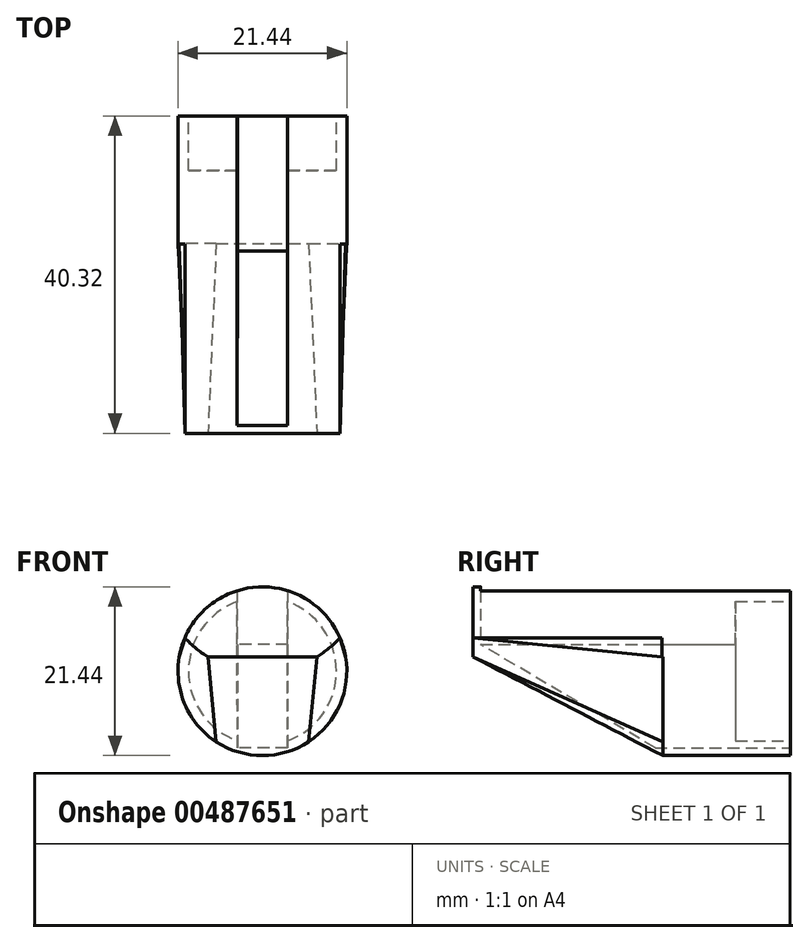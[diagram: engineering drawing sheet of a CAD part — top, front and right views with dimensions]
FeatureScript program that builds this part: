
annotation { "Feature Type Name" : "Feature", "Feature Type Description" : "" }
export const myFeature = defineFeature(function(context is Context, id is Id, definition is map)
    precondition{}
    {
        {
            var Q0;
            Q0=qCreatedBy(makeId("Front.planeOp"),FACE);
            var sketch = newSketch(context, id + "F0", { "sketchPlane" : qUnion([Q0])});
            skCircle(sketch, "E0", {"center": v(0, 0) * mm, "radius": 10.72 * mm});
            skSolve(sketch);
        }
        {
            var Q0;
            Q0=makeQuery(id+"F0.imprint","IMPRINT",FACE,{"disambiguationData":[TD([[makeQuery(id+"F0.imprint","IMPRINT",EDGE,{"derivedFrom":sQuery(id+"F0.wireOp",EDGE,"E0")}),1.0]])]});
            extrude(context, id + "F1", {"entities" : qUnion([Q0]), "depth" : 40.32 * mm});
        }
        {
            var Q0;
            Q0=makeQuery(id+"F1.opExtrude","CAP_FACE",FACE,{"disambiguationData":[OSD([sQuery(id+"F0.wireOp",EDGE,"E0")])],"isStart":true});
            var sketch = newSketch(context, id + "F2", { "sketchPlane" : qUnion([Q0])});
            skCircle(sketch, "E1", {"center": v(0, 0) * mm, "radius": 9.4 * mm});
            skSolve(sketch);
        }
        {
            var Q0;
            Q0 = qSketchRegion(id + "F2", true);
            extrude(context, id + "F3", {"entities" : qUnion([Q0]), "operationType" : NewBodyOperationType.REMOVE, "oppositeDirection" : true, "depth" : 6.93 * mm});
        }
        {
            var Q0;
            Q0=makeQuery(id+"F1.opExtrude","CAP_FACE",FACE,{"disambiguationData":[OSD([sQuery(id+"F0.wireOp",EDGE,"E0")])],"isStart":false});
            var sketch = newSketch(context, id + "F4", { "sketchPlane" : qUnion([Q0])});
            skLineSegment(sketch, "E2", {"start": v(0, 10.72) * mm, "end": v(-22.17, 10.72) * mm, "construction": true});
            skLineSegment(sketch, "E3", {"start": v(15.58, 1.83) * mm, "end": v(-23.44, 1.83) * mm, "construction": true});
            skArc(sketch, "E4", {"start": v(-10.56, 1.83) * mm, "mid": v(0, -10.88) * mm, "end": v(10.56, 1.83) * mm});
            skLineSegment(sketch, "E5", {"start": v(10.56, 1.83) * mm, "end": v(-10.56, 1.83) * mm});
            skSolve(sketch);
        }
        {
            var Q0;
            Q0 = qSketchRegion(id + "F4", true);
            extrude(context, id + "F5", {"entities" : qUnion([Q0]), "operationType" : NewBodyOperationType.REMOVE, "oppositeDirection" : true, "depth" : 24.13 * mm});
        }
        {
            var Q0;
            Q0=makeQuery(id+"F5.boolean.opBoolean","COPY",FACE,{"derivedFrom":makeQuery(id+"F5.opExtrude","CAP_FACE",FACE,{"disambiguationData":[OSD([sQuery(id+"F4.wireOp",EDGE,"E4"),sQuery(id+"F4.wireOp",EDGE,"E5")])],"isStart":false})});
            var sketch = newSketch(context, id + "F6", { "sketchPlane" : qUnion([Q0])});
            skSolve(sketch);
        }
        {
            var Q0;
            Q0=makeQuery(id+"F1.opExtrude","CAP_FACE",FACE,{"disambiguationData":[OSD([sQuery(id+"F0.wireOp",EDGE,"E0")])],"isStart":false});
            var sketch = newSketch(context, id + "F7", { "sketchPlane" : qUnion([Q0])});
            skArc(sketch, "E6", {"start": v(6.9, 1.83) * mm, "mid": v(8.46, 2.93) * mm, "end": v(9.85, 4.24) * mm});
            skLineSegment(sketch, "E7", {"start": v(6.9, 1.83) * mm, "end": v(-6.9, 1.83) * mm});
            skLineSegment(sketch, "E8", {"start": v(-9.85, 4.24) * mm, "end": v(-13.34, 4.24) * mm});
            skLineSegment(sketch, "E9", {"start": v(-13.34, 4.24) * mm, "end": v(-13.33, 1.78) * mm});
            skLineSegment(sketch, "E10", {"start": v(-13.33, 1.78) * mm, "end": v(-6.9, 1.83) * mm});
            skLineSegment(sketch, "E11", {"start": v(9.85, 4.24) * mm, "end": v(13.02, 4.24) * mm});
            skLineSegment(sketch, "E12", {"start": v(13.02, 4.24) * mm, "end": v(13.02, 1.83) * mm});
            skLineSegment(sketch, "E13", {"start": v(13.02, 1.83) * mm, "end": v(6.9, 1.83) * mm});
            skArc(sketch, "E14.trimOffspring", {"start": v(-9.85, 4.24) * mm, "mid": v(-8.46, 2.93) * mm, "end": v(-6.9, 1.83) * mm});
            skSolve(sketch);
        }
        {
            var Q0;
            Q0 = qSketchRegion(id + "F7", true);
            extrude(context, id + "F8", {"entities" : qUnion([Q0]), "operationType" : NewBodyOperationType.REMOVE, "oppositeDirection" : true, "depth" : 24.05 * mm});
        }
        {
            var Q1;
            Q1=makeQuery(id+"F5.boolean.opBoolean","COPY",FACE,{"derivedFrom":makeQuery(id+"F5.opExtrude","CAP_FACE",FACE,{"disambiguationData":[OSD([sQuery(id+"F4.wireOp",EDGE,"E4"),sQuery(id+"F4.wireOp",EDGE,"E5")])],"isStart":false})});
            var Q2;
            Q2=makeQuery(id+"F1.opExtrude","CAP_FACE",FACE,{"disambiguationData":[OSD([sQuery(id+"F0.wireOp",EDGE,"E0")])],"isStart":false});
            loft(context, id + "F9", {"operationType" : NewBodyOperationType.ADD, "sheetProfilesArray" : [{ "sheetProfileEntities" : qUnion([Q1]) }, { "sheetProfileEntities" : qUnion([Q2]) }]});
        }
        {
            var Q1;
            Q1=makeQuery(id+"F8.boolean.opBoolean","COPY",FACE,{"derivedFrom":makeQuery(id+"F8.opExtrude","SWEPT_FACE",FACE,{"disambiguationData":[OSD([sQuery(id+"F7.wireOp",EDGE,"E14.trimOffspring")])]})});
            var Q2;
            {var subQ0=sQuery(id+"F7.wireOp",EDGE,"E14.trimOffspring");var subQ2=sQuery(id+"F7.wireOp",EDGE,"E8");var subQ3=sQuery(id+"F0.wireOp",EDGE,"E0");var subQ4=sQuery(id+"F4.wireOp",EDGE,"E5");var subQ5=sQuery(id+"F4.wireOp",EDGE,"E4");Q2=makeQuery(id+"F9.boolean.opBoolean","SPLIT",FACE,{"disambiguationData":[TD([makeQuery(id+"F8.boolean.opBoolean","COPY",FACE,{"derivedFrom":makeQuery(id+"F8.opExtrude","SWEPT_FACE",FACE,{"disambiguationData":[OSD([subQ0])]})})])],"derivedFrom":makeQuery(id+"F9.opLoft","SWEPT_FACE",FACE,{"disambiguationData":[OSD([subQ3,subQ5,subQ4,sQuery(id+"F7.wireOp",EDGE,"E6"),subQ2,sQuery(id+"F7.wireOp",EDGE,"E11"),subQ0])]})});}
            loft(context, id + "F10", {"operationType" : NewBodyOperationType.ADD, "sheetProfilesArray" : [{ "sheetProfileEntities" : qUnion([Q1]) }, { "sheetProfileEntities" : qUnion([Q2]) }]});
        }
        {
            var Q1;
            {var subQ0=sQuery(id+"F7.wireOp",EDGE,"E6");var subQ1=sQuery(id+"F0.wireOp",EDGE,"E0");var subQ3=sQuery(id+"F7.wireOp",EDGE,"E11");var subQ4=sQuery(id+"F7.wireOp",EDGE,"E14.trimOffspring");var subQ5=sQuery(id+"F4.wireOp",EDGE,"E5");var subQ6=sQuery(id+"F4.wireOp",EDGE,"E4");Q1=makeQuery(id+"F9.boolean.opBoolean","SPLIT",FACE,{"disambiguationData":[TD([makeQuery(id+"F8.boolean.opBoolean","COPY",FACE,{"derivedFrom":makeQuery(id+"F8.opExtrude","SWEPT_FACE",FACE,{"disambiguationData":[OSD([subQ0])]})})])],"derivedFrom":makeQuery(id+"F9.opLoft","SWEPT_FACE",FACE,{"disambiguationData":[OSD([subQ1,subQ6,subQ5,subQ0,sQuery(id+"F7.wireOp",EDGE,"E8"),subQ3,subQ4])]})});}
            var Q2;
            Q2=makeQuery(id+"F8.boolean.opBoolean","COPY",VERTEX,{"derivedFrom":makeQuery(id+"F8.opExtrude","CAP_VERTEX",VERTEX,{"disambiguationData":[OSD([sQuery(id+"F0.wireOp",EDGE,"E0"),sQuery(id+"F7.wireOp",EDGE,"E6"),sQuery(id+"F7.wireOp",EDGE,"E11")])],"isStart":false})});
            loft(context, id + "F11", {"operationType" : NewBodyOperationType.ADD, "sheetProfilesArray" : [{ "sheetProfileEntities" : qUnion([Q1]) }, { "sheetProfileEntities" : qUnion([Q2]) }]});
        }
        {
            var Q0;
            Q0=makeQuery(id+"F1.opExtrude","CAP_FACE",FACE,{"disambiguationData":[OSD([sQuery(id+"F0.wireOp",EDGE,"E0")])],"isStart":true});
            var sketch = newSketch(context, id + "F12", { "sketchPlane" : qUnion([Q0])});
            skLineSegment(sketch, "E15.bottom", {"start": v(-3.17, 12.09) * mm, "end": v(3.17, 12.09) * mm});
            skLineSegment(sketch, "E15.top", {"start": v(-3.17, -9.71) * mm, "end": v(3.18, -9.71) * mm});
            skLineSegment(sketch, "E15.left", {"start": v(-3.17, 12.09) * mm, "end": v(-3.17, -9.71) * mm});
            skLineSegment(sketch, "E15.right", {"start": v(3.17, 12.09) * mm, "end": v(3.18, -9.71) * mm});
            skLineSegment(sketch, "E16", {"start": v(0, 0) * mm, "end": v(0, 19.8) * mm, "construction": true});
            skSolve(sketch);
        }
        {
            var Q0;
            Q0 = qSketchRegion(id + "F12", true);
            extrude(context, id + "F13", {"entities" : qUnion([Q0]), "operationType" : NewBodyOperationType.REMOVE, "oppositeDirection" : true, "depth" : 17.14 * mm});
        }
        {
            var Q0;
            {var subQ0=sQuery(id+"F4.wireOp",EDGE,"E5");Q0=makeQuery(id+"F6.imprint","IMPRINT",FACE,{"disambiguationData":[TD([[makeQuery(id+"F6.imprint","IMPRINT",EDGE,{"derivedFrom":makeQuery(id+"F5.boolean.opBoolean","COPY",EDGE,{"derivedFrom":makeQuery(id+"F5.opExtrude","CAP_EDGE",EDGE,{"disambiguationData":[OSD([subQ0])],"isStart":false})})}),1.0]])]});}
            var sketch = newSketch(context, id + "F14", { "sketchPlane" : qUnion([Q0])});
            skLineSegment(sketch, "E17", {"start": v(0, 0) * mm, "end": v(0, 12.88) * mm, "construction": true});
            skLineSegment(sketch, "E18.bottom", {"start": v(0, 10.94) * mm, "end": v(-3.21, 10.94) * mm});
            skLineSegment(sketch, "E18.top", {"start": v(0, 3.38) * mm, "end": v(-3.21, 3.38) * mm});
            skLineSegment(sketch, "E18.left", {"start": v(0, 10.94) * mm, "end": v(0, 3.38) * mm});
            skLineSegment(sketch, "E18.right", {"start": v(-3.21, 10.94) * mm, "end": v(-3.21, 3.38) * mm});
            skLineSegment(sketch, "E19.MirrorCS", {"start": v(0, 3.38) * mm, "end": v(3.21, 3.38) * mm});
            skLineSegment(sketch, "E20.MirrorCS", {"start": v(3.21, 10.94) * mm, "end": v(3.21, 3.38) * mm});
            skLineSegment(sketch, "E21.MirrorCS", {"start": v(0, 10.94) * mm, "end": v(3.21, 10.94) * mm});
            skSolve(sketch);
        }
        {
            var Q0;
            Q0 = qSketchRegion(id + "F14", true);
            extrude(context, id + "F15", {"entities" : qUnion([Q0]), "operationType" : NewBodyOperationType.REMOVE, "depth" : 23.14 * mm});
        }
        {
            var Q0;
            Q0 = qSketchRegion(id + "F14", true);
            extrude(context, id + "F16", {"entities" : qUnion([Q0]), "operationType" : NewBodyOperationType.REMOVE, "oppositeDirection" : true, "depth" : 25.4 * mm});
        }
        {
            var Q1;
            Q1=makeQuery(id+"F13.boolean.opBoolean","COPY",FACE,{"derivedFrom":makeQuery(id+"F13.opExtrude","CAP_FACE",FACE,{"disambiguationData":[OSD([sQuery(id+"F12.wireOp",EDGE,"E15.bottom"),sQuery(id+"F12.wireOp",EDGE,"E15.top"),sQuery(id+"F12.wireOp",EDGE,"E15.left"),sQuery(id+"F12.wireOp",EDGE,"E15.right")])],"isStart":false})});
            var Q2;
            Q2=makeQuery(id+"F15.boolean.opBoolean","COPY",FACE,{"derivedFrom":makeQuery(id+"F15.opExtrude","CAP_FACE",FACE,{"disambiguationData":[OSD([sQuery(id+"F14.wireOp",EDGE,"E18.bottom"),sQuery(id+"F14.wireOp",EDGE,"E18.top"),sQuery(id+"F14.wireOp",EDGE,"E18.right"),sQuery(id+"F14.wireOp",EDGE,"E19.MirrorCS"),sQuery(id+"F14.wireOp",EDGE,"E21.MirrorCS"),sQuery(id+"F14.wireOp",EDGE,"E20.MirrorCS")])],"isStart":false})});
            loft(context, id + "F17", {"operationType" : NewBodyOperationType.REMOVE, "sheetProfilesArray" : [{ "sheetProfileEntities" : qUnion([Q1]) }, { "sheetProfileEntities" : qUnion([Q2]) }]});
        }
    });
